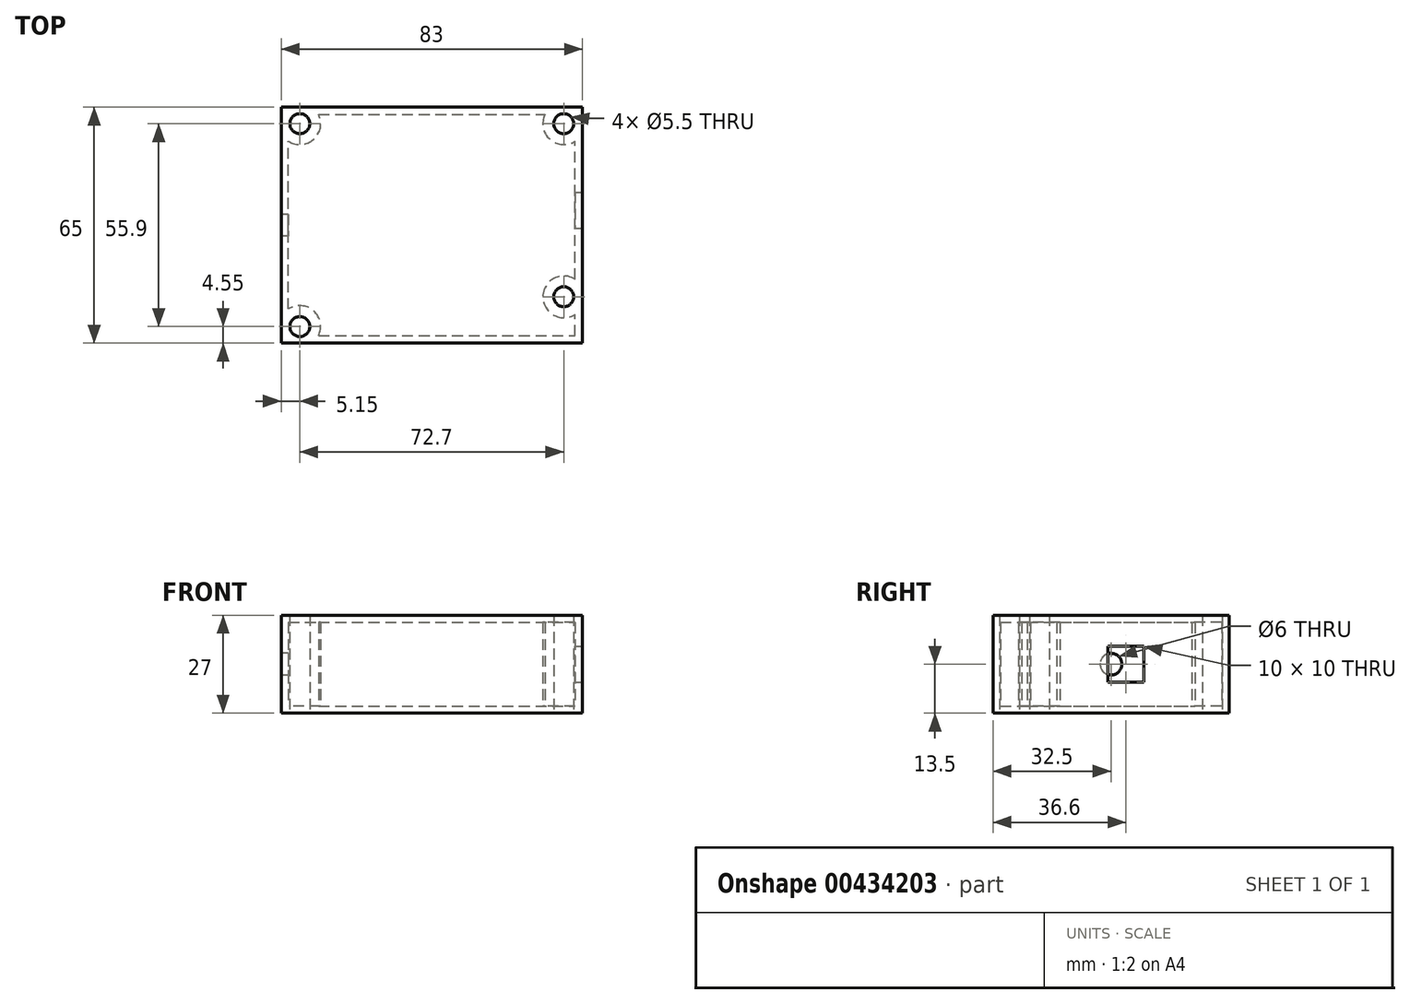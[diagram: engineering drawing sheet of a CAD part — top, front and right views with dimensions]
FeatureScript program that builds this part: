
annotation { "Feature Type Name" : "Feature", "Feature Type Description" : "" }
export const myFeature = defineFeature(function(context is Context, id is Id, definition is map)
    precondition{}
    {
        {
            var Q0;
            Q0=qCreatedBy(makeId("Top.planeOp"),FACE);
            var sketch = newSketch(context, id + "F0", { "sketchPlane" : qUnion([Q0])});
            skLineSegment(sketch, "E0.bottom", {"start": v(41.5, -32.5) * mm, "end": v(-41.5, -32.5) * mm});
            skLineSegment(sketch, "E0.top", {"start": v(41.5, 32.5) * mm, "end": v(-41.5, 32.5) * mm});
            skLineSegment(sketch, "E0.left", {"start": v(41.5, -32.5) * mm, "end": v(41.5, 32.5) * mm});
            skLineSegment(sketch, "E0.right", {"start": v(-41.5, -32.5) * mm, "end": v(-41.5, 32.5) * mm});
            skPoint(sketch, "E0.middle", {"position": v(0, 0) * mm});
            skSolve(sketch);
        }
        {
            var Q0;
            Q0=qSketchRegion(id+"F0",true);
            extrude(context, id + "F1", {"entities" : qUnion([Q0]), "depth" : 2 * mm});
        }
        {
            var Q0;
            Q0=makeQuery(id+"F1.opExtrude","CAP_FACE",FACE,{"disambiguationData":[OSD([sQuery(id+"F0.wireOp",EDGE,"E0.bottom"),sQuery(id+"F0.wireOp",EDGE,"E0.top"),sQuery(id+"F0.wireOp",EDGE,"E0.left"),sQuery(id+"F0.wireOp",EDGE,"E0.right")])],"isStart":false});
            var sketch = newSketch(context, id + "F2", { "sketchPlane" : qUnion([Q0])});
            skCircle(sketch, "E1", {"center": v(-36.35, -27.95) * mm, "radius": 2.75 * mm});
            skCircle(sketch, "E2", {"center": v(-36.35, 27.95) * mm, "radius": 2.75 * mm});
            skCircle(sketch, "E3", {"center": v(36.35, 27.95) * mm, "radius": 2.75 * mm});
            skCircle(sketch, "E4", {"center": v(36.35, -19.75) * mm, "radius": 2.75 * mm});
            skArc(sketch, "E5.0", {"start": v(-31.2, -30.5) * mm, "mid": v(-32.54, -23.65) * mm, "end": v(-39.5, -23.14) * mm});
            skArc(sketch, "E6.0", {"start": v(-39.5, 23.14) * mm, "mid": v(-32.54, 23.65) * mm, "end": v(-31.2, 30.5) * mm});
            skArc(sketch, "E7.0", {"start": v(39.5, -14.94) * mm, "mid": v(30.6, -19.75) * mm, "end": v(39.5, -24.56) * mm});
            skLineSegment(sketch, "E8.bottom", {"start": v(-41.5, -32.5) * mm, "end": v(41.5, -32.5) * mm});
            skLineSegment(sketch, "E8.top", {"start": v(-41.5, 32.5) * mm, "end": v(41.5, 32.5) * mm});
            skLineSegment(sketch, "E8.left", {"start": v(-41.5, -32.5) * mm, "end": v(-41.5, 32.5) * mm});
            skLineSegment(sketch, "E8.right", {"start": v(41.5, -32.5) * mm, "end": v(41.5, 32.5) * mm});
            skLineSegment(sketch, "E9.0", {"start": v(-39.5, -23.14) * mm, "end": v(-39.5, 23.14) * mm});
            skLineSegment(sketch, "E9.2", {"start": v(39.5, -30.5) * mm, "end": v(39.5, -24.56) * mm});
            skLineSegment(sketch, "E9.3", {"start": v(-31.2, 30.5) * mm, "end": v(31.2, 30.5) * mm});
            skLineSegment(sketch, "E10.trimOffspring", {"start": v(-31.2, -30.5) * mm, "end": v(39.5, -30.5) * mm});
            skArc(sketch, "E11.trimOffspring", {"start": v(31.2, 30.5) * mm, "mid": v(32.54, 23.65) * mm, "end": v(39.5, 23.14) * mm});
            skLineSegment(sketch, "E12.trimOffspring", {"start": v(39.5, -14.94) * mm, "end": v(39.5, 23.14) * mm});
            skSolve(sketch);
        }
        {
            var Q0;
            Q0=qSketchRegion(id+"F2",true);
            extrude(context, id + "F3", {"entities" : qUnion([Q0]), "operationType" : NewBodyOperationType.ADD, "depth" : 23 * mm});
        }
        {
            var Q0;
            Q0=makeQuery(id+"F3.boolean.opBoolean","SPLIT",FACE,{"disambiguationData":[TD([makeQuery(id+"F3.opExtrude","SWEPT_FACE",FACE,{"disambiguationData":[OSD([sQuery(id+"F2.wireOp",EDGE,"E5.0")])]})])],"derivedFrom":makeQuery(id+"F1.opExtrude","CAP_FACE",FACE,{"disambiguationData":[OSD([sQuery(id+"F0.wireOp",EDGE,"E0.bottom"),sQuery(id+"F0.wireOp",EDGE,"E0.top"),sQuery(id+"F0.wireOp",EDGE,"E0.left"),sQuery(id+"F0.wireOp",EDGE,"E0.right")])],"isStart":false})});
            var sketch = newSketch(context, id + "F4", { "sketchPlane" : qUnion([Q0])});
            skCircle(sketch, "E13", {"center": v(-36.35, 27.95) * mm, "radius": 2.75 * mm});
            skCircle(sketch, "E14", {"center": v(-36.35, -27.95) * mm, "radius": 2.75 * mm});
            skCircle(sketch, "E15", {"center": v(36.35, 27.95) * mm, "radius": 2.75 * mm});
            skCircle(sketch, "E16", {"center": v(36.35, -19.75) * mm, "radius": 2.75 * mm});
            skSolve(sketch);
        }
        {
            var Q0;
            Q0=qSketchRegion(id+"F4",true);
            extrude(context, id + "F5", {"entities" : qUnion([Q0]), "operationType" : NewBodyOperationType.REMOVE, "endBound" : BoundingType.THROUGH_ALL, "oppositeDirection" : true, "depth" : 25 * mm});
        }
        {
            var Q0;
            Q0=makeQuery(id+"F3.opExtrude","CAP_FACE",FACE,{"disambiguationData":[OSD([sQuery(id+"F2.wireOp",EDGE,"E1"),sQuery(id+"F2.wireOp",EDGE,"E2"),sQuery(id+"F2.wireOp",EDGE,"E3"),sQuery(id+"F2.wireOp",EDGE,"E4"),sQuery(id+"F2.wireOp",EDGE,"E5.0"),sQuery(id+"F2.wireOp",EDGE,"E6.0"),sQuery(id+"F2.wireOp",EDGE,"E7.0"),sQuery(id+"F2.wireOp",EDGE,"E8.bottom"),sQuery(id+"F2.wireOp",EDGE,"E8.top"),sQuery(id+"F2.wireOp",EDGE,"E8.left"),sQuery(id+"F2.wireOp",EDGE,"E8.right"),sQuery(id+"F2.wireOp",EDGE,"E9.0"),sQuery(id+"F2.wireOp",EDGE,"E9.2"),sQuery(id+"F2.wireOp",EDGE,"E9.3"),sQuery(id+"F2.wireOp",EDGE,"E10.trimOffspring"),sQuery(id+"F2.wireOp",EDGE,"E11.trimOffspring"),sQuery(id+"F2.wireOp",EDGE,"E12.trimOffspring")])],"isStart":false});
            var sketch = newSketch(context, id + "F6", { "sketchPlane" : qUnion([Q0])});
            skLineSegment(sketch, "E17.bottom", {"start": v(-41.5, -32.5) * mm, "end": v(41.5, -32.5) * mm});
            skLineSegment(sketch, "E17.top", {"start": v(-41.5, 32.5) * mm, "end": v(41.5, 32.5) * mm});
            skLineSegment(sketch, "E17.left", {"start": v(-41.5, -32.5) * mm, "end": v(-41.5, 32.5) * mm});
            skLineSegment(sketch, "E17.right", {"start": v(41.5, -32.5) * mm, "end": v(41.5, 32.5) * mm});
            skCircle(sketch, "E18", {"center": v(-36.35, -27.95) * mm, "radius": 2.75 * mm});
            skCircle(sketch, "E19", {"center": v(-36.35, 27.95) * mm, "radius": 2.75 * mm});
            skCircle(sketch, "E20", {"center": v(36.35, 27.95) * mm, "radius": 2.75 * mm});
            skCircle(sketch, "E21", {"center": v(36.35, -19.75) * mm, "radius": 2.75 * mm});
            skSolve(sketch);
        }
        {
            var Q0;
            Q0=qSketchRegion(id+"F6",true);
            extrude(context, id + "F7", {"entities" : qUnion([Q0]), "operationType" : NewBodyOperationType.ADD, "depth" : 2 * mm});
        }
        {
            var Q0;
            Q0=makeQuery(id+"F7.boolean.opBoolean","MERGE",FACE,{"derivedFrom":[makeQuery(id+"F3.boolean.opBoolean","MERGE",FACE,{"derivedFrom":[makeQuery(id+"F1.opExtrude","SWEPT_FACE",FACE,{"disambiguationData":[OSD([sQuery(id+"F0.wireOp",EDGE,"E0.left")])]}),makeQuery(id+"F3.opExtrude","SWEPT_FACE",FACE,{"disambiguationData":[OSD([sQuery(id+"F2.wireOp",EDGE,"E8.right")])]})]}),makeQuery(id+"F7.opExtrude","SWEPT_FACE",FACE,{"disambiguationData":[OSD([sQuery(id+"F6.wireOp",EDGE,"E17.right")])]})]});
            var sketch = newSketch(context, id + "F8", { "sketchPlane" : qUnion([Q0])});
            skLineSegment(sketch, "E22.bottom", {"start": v(9.1, 8.5) * mm, "end": v(-0.9, 8.5) * mm});
            skLineSegment(sketch, "E22.top", {"start": v(9.1, 18.5) * mm, "end": v(-0.9, 18.5) * mm});
            skLineSegment(sketch, "E22.left", {"start": v(9.1, 8.5) * mm, "end": v(9.1, 18.5) * mm});
            skLineSegment(sketch, "E22.right", {"start": v(-0.9, 8.5) * mm, "end": v(-0.9, 18.5) * mm});
            skPoint(sketch, "E22.middle", {"position": v(4.1, 13.5) * mm});
            skSolve(sketch);
        }
        {
            var Q0;
            Q0=qSketchRegion(id+"F8",true);
            extrude(context, id + "F9", {"entities" : qUnion([Q0]), "operationType" : NewBodyOperationType.REMOVE, "oppositeDirection" : true, "depth" : 2 * mm});
        }
        {
            var Q0;
            Q0=makeQuery(id+"F7.boolean.opBoolean","MERGE",FACE,{"derivedFrom":[makeQuery(id+"F3.boolean.opBoolean","MERGE",FACE,{"derivedFrom":[makeQuery(id+"F1.opExtrude","SWEPT_FACE",FACE,{"disambiguationData":[OSD([sQuery(id+"F0.wireOp",EDGE,"E0.right")])]}),makeQuery(id+"F3.opExtrude","SWEPT_FACE",FACE,{"disambiguationData":[OSD([sQuery(id+"F2.wireOp",EDGE,"E8.left")])]})]}),makeQuery(id+"F7.opExtrude","SWEPT_FACE",FACE,{"disambiguationData":[OSD([sQuery(id+"F6.wireOp",EDGE,"E17.left")])]})]});
            var sketch = newSketch(context, id + "F10", { "sketchPlane" : qUnion([Q0])});
            skCircle(sketch, "E23", {"center": v(0, 13.5) * mm, "radius": 3 * mm});
            skSolve(sketch);
        }
        {
            var Q0;
            Q0=qSketchRegion(id+"F10",true);
            extrude(context, id + "F11", {"entities" : qUnion([Q0]), "operationType" : NewBodyOperationType.REMOVE, "oppositeDirection" : true, "depth" : 2 * mm});
        }
    });
